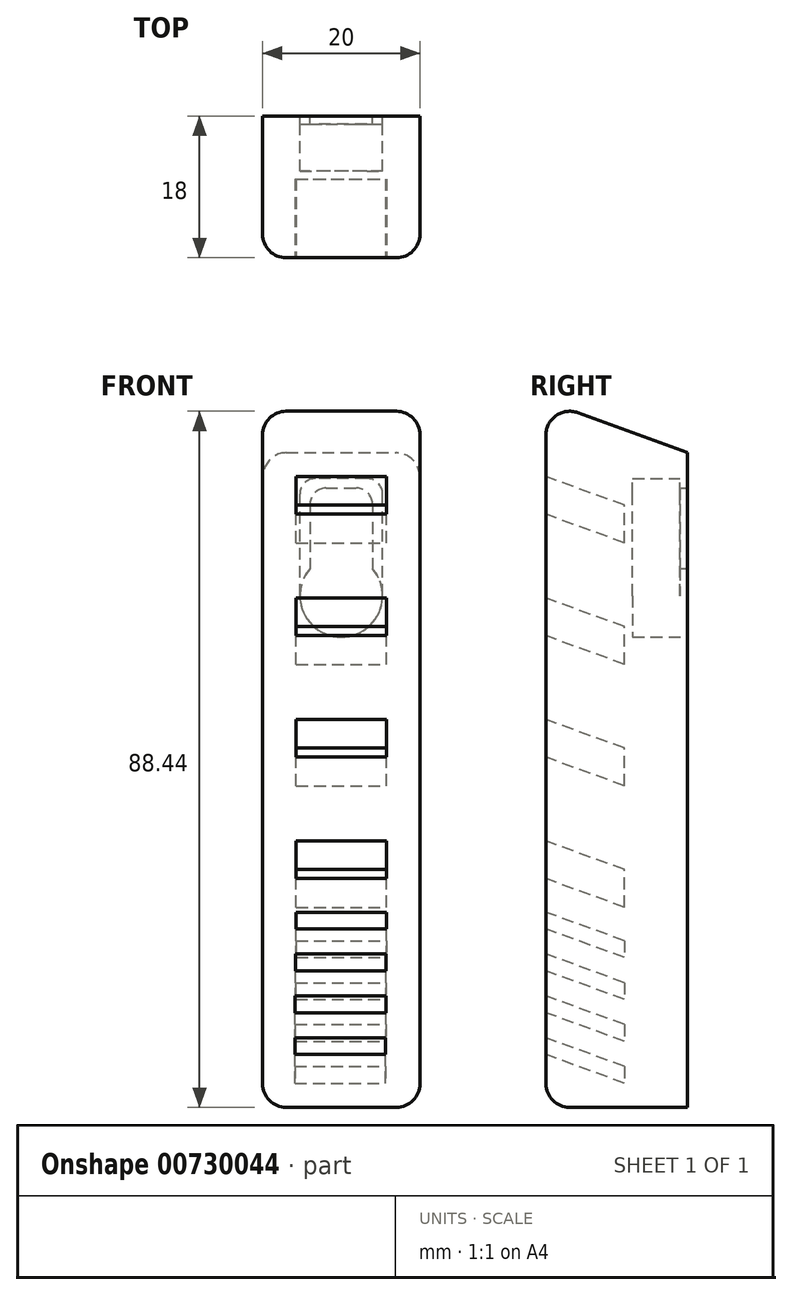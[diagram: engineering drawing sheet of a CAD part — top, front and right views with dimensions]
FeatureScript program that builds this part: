
annotation { "Feature Type Name" : "Feature", "Feature Type Description" : "" }
export const myFeature = defineFeature(function(context is Context, id is Id, definition is map)
    precondition{}
    {
        {
            var Q0;
            Q0=qCreatedBy(makeId("Front.planeOp"),FACE);
            var sketch = newSketch(context, id + "F0", { "sketchPlane" : qUnion([Q0])});
            skLineSegment(sketch, "E0.bottom", {"start": v(10, 45) * mm, "end": v(-10, 45) * mm});
            skLineSegment(sketch, "E0.top", {"start": v(10, -45) * mm, "end": v(-10, -45) * mm});
            skLineSegment(sketch, "E0.left", {"start": v(10, 45) * mm, "end": v(10, -45) * mm});
            skLineSegment(sketch, "E0.right", {"start": v(-10, 45) * mm, "end": v(-10, -45) * mm});
            skPoint(sketch, "E0.middle", {"position": v(0, 0) * mm});
            skSolve(sketch);
        }
        {
            var Q0;
            Q0 = qSketchRegion(id + "F0", true);
            extrude(context, id + "F1", {"entities" : qUnion([Q0]), "depth" : 18 * mm, "offsetDistance" : 25 * mm});
        }
        {
            var Q0;
            Q0=makeQuery(id+"F1.opExtrude","CAP_EDGE",EDGE,{"disambiguationData":[OSD([sQuery(id+"F0.wireOp",EDGE,"E0.bottom")])],"isStart":false});
            var Q1;
            Q1=makeQuery(id+"F1.opExtrude","CAP_FACE",FACE,{"disambiguationData":[OSD([sQuery(id+"F0.wireOp",EDGE,"E0.bottom"),sQuery(id+"F0.wireOp",EDGE,"E0.top"),sQuery(id+"F0.wireOp",EDGE,"E0.left"),sQuery(id+"F0.wireOp",EDGE,"E0.right")])],"isStart":false});
            cPlane(context, id + "F2", {"entities" : qUnion([Q0, Q1]), "cplaneType" : CPlaneType.LINE_ANGLE, "offset" : 25 * mm, "angle" : 20 * degree, "width" : 150 * mm, "height" : 150 * mm});
        }
        {
            var Q0;
            Q0=makeQuery(id+"F1.opExtrude","CAP_FACE",FACE,{"disambiguationData":[OSD([sQuery(id+"F0.wireOp",EDGE,"E0.bottom"),sQuery(id+"F0.wireOp",EDGE,"E0.top"),sQuery(id+"F0.wireOp",EDGE,"E0.left"),sQuery(id+"F0.wireOp",EDGE,"E0.right")])],"isStart":false});
            var sketch = newSketch(context, id + "F3", { "sketchPlane" : qUnion([Q0])});
            skLineSegment(sketch, "E1", {"start": v(0, 45) * mm, "end": v(0, 32.75) * mm, "construction": true});
            skLineSegment(sketch, "E2", {"start": v(0, -45) * mm, "end": v(0, -32.75) * mm, "construction": true});
            skSolve(sketch);
        }
        {
            var Q0;
            Q0=qCreatedBy(id+"F2.planeOp",FACE);
            var sketch = newSketch(context, id + "F4", { "sketchPlane" : qUnion([Q0])});
            skPoint(sketch, "E3", {"position": v(0, 24.62) * mm});
            skLineSegment(sketch, "E4.bottom", {"start": v(-5.75, 26.87) * mm, "end": v(5.75, 26.87) * mm});
            skLineSegment(sketch, "E4.top", {"start": v(-5.75, 22.37) * mm, "end": v(5.75, 22.37) * mm});
            skLineSegment(sketch, "E4.left", {"start": v(-5.75, 26.87) * mm, "end": v(-5.75, 22.37) * mm});
            skLineSegment(sketch, "E4.right", {"start": v(5.75, 26.87) * mm, "end": v(5.75, 22.37) * mm});
            skLineSegment(sketch, "E5.1.0.0", {"start": v(5.75, 12.37) * mm, "end": v(5.75, 7.87) * mm});
            skLineSegment(sketch, "E5.1.0.1", {"start": v(-5.75, 12.37) * mm, "end": v(5.75, 12.37) * mm});
            skLineSegment(sketch, "E5.1.0.2", {"start": v(-5.75, 12.37) * mm, "end": v(-5.75, 7.87) * mm});
            skLineSegment(sketch, "E5.1.0.3", {"start": v(-5.75, 7.87) * mm, "end": v(5.75, 7.87) * mm});
            skLineSegment(sketch, "E5.2.0.0", {"start": v(5.75, -2.13) * mm, "end": v(5.75, -6.63) * mm});
            skLineSegment(sketch, "E5.2.0.1", {"start": v(-5.75, -2.13) * mm, "end": v(5.75, -2.13) * mm});
            skLineSegment(sketch, "E5.2.0.2", {"start": v(-5.75, -2.13) * mm, "end": v(-5.75, -6.63) * mm});
            skLineSegment(sketch, "E5.2.0.3", {"start": v(-5.75, -6.63) * mm, "end": v(5.75, -6.63) * mm});
            skLineSegment(sketch, "E5.direction1", {"start": v(5.75, 22.37) * mm, "end": v(5.75, 7.87) * mm, "construction": true});
            skLineSegment(sketch, "E6.0.3.0", {"start": v(5.75, -16.63) * mm, "end": v(5.75, -21.13) * mm});
            skLineSegment(sketch, "E6.3.3.0", {"start": v(-5.75, -16.63) * mm, "end": v(5.75, -16.63) * mm});
            skLineSegment(sketch, "E6.6.3.0", {"start": v(-5.75, -16.63) * mm, "end": v(-5.75, -21.13) * mm});
            skLineSegment(sketch, "E6.9.3.0", {"start": v(-5.75, -21.13) * mm, "end": v(5.75, -21.13) * mm});
            skLineSegment(sketch, "E7", {"start": v(0, -21.13) * mm, "end": v(0, -26.13) * mm, "construction": true});
            skLineSegment(sketch, "E8.bottom", {"start": v(-5.75, -27.13) * mm, "end": v(5.75, -27.13) * mm});
            skLineSegment(sketch, "E8.top", {"start": v(-5.75, -25.13) * mm, "end": v(5.75, -25.13) * mm});
            skLineSegment(sketch, "E8.left", {"start": v(-5.75, -27.13) * mm, "end": v(-5.75, -25.13) * mm});
            skLineSegment(sketch, "E8.right", {"start": v(5.75, -27.13) * mm, "end": v(5.75, -25.13) * mm});
            skPoint(sketch, "E8.middle", {"position": v(0, -26.13) * mm});
            skLineSegment(sketch, "E9.1.0.0", {"start": v(5.8, -32.13) * mm, "end": v(5.8, -30.13) * mm});
            skLineSegment(sketch, "E9.1.0.1", {"start": v(-5.7, -30.13) * mm, "end": v(5.8, -30.13) * mm});
            skLineSegment(sketch, "E9.1.0.2", {"start": v(-5.7, -32.13) * mm, "end": v(-5.7, -30.13) * mm});
            skLineSegment(sketch, "E9.1.0.3", {"start": v(-5.7, -32.13) * mm, "end": v(5.8, -32.13) * mm});
            skLineSegment(sketch, "E9.2.0.0", {"start": v(5.85, -37.13) * mm, "end": v(5.85, -35.13) * mm});
            skLineSegment(sketch, "E9.2.0.1", {"start": v(-5.65, -35.13) * mm, "end": v(5.85, -35.13) * mm});
            skLineSegment(sketch, "E9.2.0.2", {"start": v(-5.65, -37.13) * mm, "end": v(-5.65, -35.13) * mm});
            skLineSegment(sketch, "E9.2.0.3", {"start": v(-5.65, -37.13) * mm, "end": v(5.85, -37.13) * mm});
            skLineSegment(sketch, "E9.3.0.0", {"start": v(5.9, -42.13) * mm, "end": v(5.9, -40.13) * mm});
            skLineSegment(sketch, "E9.3.0.1", {"start": v(-5.6, -40.13) * mm, "end": v(5.9, -40.13) * mm});
            skLineSegment(sketch, "E9.3.0.2", {"start": v(-5.6, -42.13) * mm, "end": v(-5.6, -40.13) * mm});
            skLineSegment(sketch, "E9.3.0.3", {"start": v(-5.6, -42.13) * mm, "end": v(5.9, -42.13) * mm});
            skLineSegment(sketch, "E9.direction1", {"start": v(5.75, -27.13) * mm, "end": v(5.8, -32.13) * mm, "construction": true});
            skSolve(sketch);
        }
        {
            var Q0;
            Q0=makeQuery(id+"F3.imprint","IMPRINT",FACE,{"disambiguationData":[TD([[makeQuery(id+"F3.imprint","IMPRINT",EDGE,{"derivedFrom":makeQuery(id+"F1.opExtrude","CAP_EDGE",EDGE,{"disambiguationData":[OSD([sQuery(id+"F0.wireOp",EDGE,"E0.bottom")])],"isStart":false})}),1.0]])]});
            cPlane(context, id + "F5", {"entities" : qUnion([Q0]), "cplaneType" : CPlaneType.OFFSET, "offset" : 10 * mm, "oppositeDirection" : true, "width" : 150 * mm, "height" : 150 * mm});
        }
        {
            var Q0;
            Q0=makeQuery(id+"F4.imprint","IMPRINT",FACE,{"disambiguationData":[TD([[makeQuery(id+"F4.imprint","IMPRINT",EDGE,{"derivedFrom":sQuery(id+"F4.wireOp",EDGE,"E4.bottom")}),-1.0]])]});
            var Q1;
            Q1=makeQuery(id+"F4.imprint","IMPRINT",FACE,{"disambiguationData":[TD([[makeQuery(id+"F4.imprint","IMPRINT",EDGE,{"derivedFrom":sQuery(id+"F4.wireOp",EDGE,"E5.1.0.0")}),-1.0]])]});
            var Q2;
            Q2=makeQuery(id+"F4.imprint","IMPRINT",FACE,{"disambiguationData":[TD([[makeQuery(id+"F4.imprint","IMPRINT",EDGE,{"derivedFrom":sQuery(id+"F4.wireOp",EDGE,"E5.2.0.0")}),-1.0]])]});
            var Q3;
            Q3=makeQuery(id+"F4.imprint","IMPRINT",FACE,{"disambiguationData":[TD([[makeQuery(id+"F4.imprint","IMPRINT",EDGE,{"derivedFrom":sQuery(id+"F4.wireOp",EDGE,"E6.0.3.0")}),-1.0]])]});
            var Q4;
            Q4=makeQuery(id+"F4.imprint","IMPRINT",FACE,{"disambiguationData":[TD([[makeQuery(id+"F4.imprint","IMPRINT",EDGE,{"derivedFrom":sQuery(id+"F4.wireOp",EDGE,"E8.bottom")}),1.0]])]});
            var Q5;
            Q5=makeQuery(id+"F4.imprint","IMPRINT",FACE,{"disambiguationData":[TD([[makeQuery(id+"F4.imprint","IMPRINT",EDGE,{"derivedFrom":sQuery(id+"F4.wireOp",EDGE,"E9.1.0.0")}),1.0]])]});
            var Q6;
            Q6=makeQuery(id+"F4.imprint","IMPRINT",FACE,{"disambiguationData":[TD([[makeQuery(id+"F4.imprint","IMPRINT",EDGE,{"derivedFrom":sQuery(id+"F4.wireOp",EDGE,"E9.2.0.0")}),1.0]])]});
            var Q7;
            Q7=makeQuery(id+"F4.imprint","IMPRINT",FACE,{"disambiguationData":[TD([[makeQuery(id+"F4.imprint","IMPRINT",EDGE,{"derivedFrom":sQuery(id+"F4.wireOp",EDGE,"E9.3.0.0")}),1.0]])]});
            var Q8;
            Q8=qCreatedBy(id+"F5.planeOp",FACE);
            extrude(context, id + "F6", {"entities" : qUnion([Q0, Q1, Q2, Q3, Q4, Q5, Q6, Q7]), "operationType" : NewBodyOperationType.REMOVE, "endBound" : BoundingType.UP_TO_SURFACE, "depth" : 25 * mm, "endBoundEntityFace" : qUnion([Q8]), "offsetDistance" : 25 * mm});
        }
        {
            var Q0;
            Q0=makeQuery(id+"F6.boolean.opBoolean","COPY",FACE,{"derivedFrom":makeQuery(id+"F6.opExtrude","SWEPT_FACE",FACE,{"disambiguationData":[OSD([sQuery(id+"F4.wireOp",EDGE,"E4.bottom")])]})});
            cPlane(context, id + "F7", {"entities" : qUnion([Q0]), "cplaneType" : CPlaneType.OFFSET, "offset" : 9 * mm, "oppositeDirection" : true, "width" : 150 * mm, "height" : 150 * mm});
        }
        {
            var Q0;
            Q0=qCreatedBy(id+"F7.planeOp",FACE);
            var sketch = newSketch(context, id + "F8", { "sketchPlane" : qUnion([Q0])});
            skLineSegment(sketch, "E10.bottom", {"start": v(-21.78, 0) * mm, "end": v(21.78, 0) * mm});
            skLineSegment(sketch, "E10.top", {"start": v(-21.78, 43.13) * mm, "end": v(21.78, 43.13) * mm});
            skLineSegment(sketch, "E10.left", {"start": v(-21.78, 0) * mm, "end": v(-21.78, 43.13) * mm});
            skLineSegment(sketch, "E10.right", {"start": v(21.78, 0) * mm, "end": v(21.78, 43.13) * mm});
            skPoint(sketch, "E10.middle", {"position": v(0, 21.57) * mm});
            skSolve(sketch);
        }
        {
            var Q0;
            Q0=makeQuery(id+"F8.imprint","IMPRINT",FACE,{"disambiguationData":[TD([[makeQuery(id+"F8.imprint","IMPRINT",EDGE,{"derivedFrom":sQuery(id+"F8.wireOp",EDGE,"E10.bottom")}),1.0]])]});
            extrude(context, id + "F9", {"entities" : qUnion([Q0]), "operationType" : NewBodyOperationType.REMOVE, "oppositeDirection" : true, "depth" : 16.4 * mm, "offsetDistance" : 25 * mm});
        }
        {
            var Q0;
            Q0=makeQuery(id+"F1.opExtrude","CAP_EDGE",EDGE,{"disambiguationData":[OSD([sQuery(id+"F0.wireOp",EDGE,"E0.right")])],"isStart":false});
            var Q1;
            Q1=makeQuery(id+"F9.boolean.opBoolean","INTERSECT",EDGE,{"derivedFrom":[makeQuery(id+"F1.opExtrude","CAP_FACE",FACE,{"disambiguationData":[OSD([sQuery(id+"F0.wireOp",EDGE,"E0.bottom"),sQuery(id+"F0.wireOp",EDGE,"E0.top"),sQuery(id+"F0.wireOp",EDGE,"E0.left"),sQuery(id+"F0.wireOp",EDGE,"E0.right")])],"isStart":false}),makeQuery(id+"F9.opExtrude","CAP_FACE",FACE,{"disambiguationData":[OSD([sQuery(id+"F8.wireOp",EDGE,"E10.bottom"),sQuery(id+"F8.wireOp",EDGE,"E10.top"),sQuery(id+"F8.wireOp",EDGE,"E10.left"),sQuery(id+"F8.wireOp",EDGE,"E10.right")])],"isStart":true})]});
            var Q2;
            Q2=makeQuery(id+"F1.opExtrude","CAP_EDGE",EDGE,{"disambiguationData":[OSD([sQuery(id+"F0.wireOp",EDGE,"E0.left")])],"isStart":false});
            var Q3;
            Q3=makeQuery(id+"F1.opExtrude","CAP_EDGE",EDGE,{"disambiguationData":[OSD([sQuery(id+"F0.wireOp",EDGE,"E0.top")])],"isStart":false});
            var Q4;
            Q4=makeQuery(id+"F9.boolean.opBoolean","INTERSECT",EDGE,{"derivedFrom":[makeQuery(id+"F1.opExtrude","SWEPT_FACE",FACE,{"disambiguationData":[OSD([sQuery(id+"F0.wireOp",EDGE,"E0.right")])]}),makeQuery(id+"F9.opExtrude","CAP_FACE",FACE,{"disambiguationData":[OSD([sQuery(id+"F8.wireOp",EDGE,"E10.bottom"),sQuery(id+"F8.wireOp",EDGE,"E10.top"),sQuery(id+"F8.wireOp",EDGE,"E10.left"),sQuery(id+"F8.wireOp",EDGE,"E10.right")])],"isStart":true})]});
            var Q5;
            Q5=makeQuery(id+"F9.boolean.opBoolean","INTERSECT",EDGE,{"derivedFrom":[makeQuery(id+"F1.opExtrude","SWEPT_FACE",FACE,{"disambiguationData":[OSD([sQuery(id+"F0.wireOp",EDGE,"E0.left")])]}),makeQuery(id+"F9.opExtrude","CAP_FACE",FACE,{"disambiguationData":[OSD([sQuery(id+"F8.wireOp",EDGE,"E10.bottom"),sQuery(id+"F8.wireOp",EDGE,"E10.top"),sQuery(id+"F8.wireOp",EDGE,"E10.left"),sQuery(id+"F8.wireOp",EDGE,"E10.right")])],"isStart":true})]});
            var Q6;
            Q6=makeQuery(id+"F1.opExtrude","SWEPT_EDGE",EDGE,{"disambiguationData":[OSD([sQuery(id+"F0.wireOp",EDGE,"E0.top"),sQuery(id+"F0.wireOp",EDGE,"E0.right")])]});
            var Q7;
            Q7=makeQuery(id+"F1.opExtrude","SWEPT_EDGE",EDGE,{"disambiguationData":[OSD([sQuery(id+"F0.wireOp",EDGE,"E0.top"),sQuery(id+"F0.wireOp",EDGE,"E0.left")])]});
            fillet(context, id + "F10", {"entities" : qUnion([Q0, Q1, Q2, Q3, Q4, Q5, Q6, Q7]), "radius" : 3 * mm, "tangentPropagation" : true, "allowEdgeOverflow" : false});
        }
        {
            var Q0;
            Q0=makeQuery(id+"F1.opExtrude","CAP_FACE",FACE,{"disambiguationData":[OSD([sQuery(id+"F0.wireOp",EDGE,"E0.bottom"),sQuery(id+"F0.wireOp",EDGE,"E0.top"),sQuery(id+"F0.wireOp",EDGE,"E0.left"),sQuery(id+"F0.wireOp",EDGE,"E0.right")])],"isStart":true});
            var sketch = newSketch(context, id + "F11", { "sketchPlane" : qUnion([Q0])});
            skCircle(sketch, "E11", {"center": v(0, 20) * mm, "radius": 5.25 * mm});
            skLineSegment(sketch, "E12.bottom", {"start": v(1.96, 33.68) * mm, "end": v(-1.96, 33.68) * mm});
            skLineSegment(sketch, "E12.left", {"start": v(3.96, 31.68) * mm, "end": v(3.96, 23.45) * mm});
            skLineSegment(sketch, "E12.right", {"start": v(-3.96, 31.68) * mm, "end": v(-3.96, 23.45) * mm});
            skPoint(sketch, "E13.visualSharp", {"position": v(-3.96, 33.68) * mm});
            skArc(sketch, "E13.filletArc", {"start": v(-1.96, 33.68) * mm, "mid": v(-3.37, 33.09) * mm, "end": v(-3.96, 31.68) * mm});
            skPoint(sketch, "E14.visualSharp", {"position": v(3.96, 33.68) * mm});
            skArc(sketch, "E14.filletArc", {"start": v(3.96, 31.68) * mm, "mid": v(3.37, 33.09) * mm, "end": v(1.96, 33.68) * mm});
            skLineSegment(sketch, "E15", {"start": v(5.25, 20) * mm, "end": v(5.25, 32.9) * mm});
            skPoint(sketch, "E16", {"position": v(5.25, 20) * mm});
            skLineSegment(sketch, "E17", {"start": v(0, 33.68) * mm, "end": v(0, 28.15) * mm, "construction": true});
            skLineSegment(sketch, "E18.MirrorCS", {"start": v(-5.25, 20) * mm, "end": v(-5.25, 32.9) * mm});
            skLineSegment(sketch, "E19", {"start": v(-3.25, 34.9) * mm, "end": v(3.25, 34.9) * mm});
            skPoint(sketch, "E20.visualSharp", {"position": v(-5.25, 34.9) * mm});
            skArc(sketch, "E20.filletArc", {"start": v(-3.25, 34.9) * mm, "mid": v(-4.66, 34.31) * mm, "end": v(-5.25, 32.9) * mm});
            skPoint(sketch, "E21.visualSharp", {"position": v(5.25, 34.9) * mm});
            skArc(sketch, "E21.filletArc", {"start": v(5.25, 32.9) * mm, "mid": v(4.66, 34.31) * mm, "end": v(3.25, 34.9) * mm});
            skSolve(sketch);
        }
        {
            var Q0;
            Q0 = qSketchRegion(id + "F11", true);
            var Q1;
            Q1=makeQuery(id+"F11.imprint","IMPRINT",FACE,{"disambiguationData":[TD([[makeQuery(id+"F11.imprint","IMPRINT",EDGE,{"derivedFrom":sQuery(id+"F11.wireOp",EDGE,"E12.bottom")}),1.0]])]});
            extrude(context, id + "F12", {"entities" : qUnion([Q0, Q1]), "operationType" : NewBodyOperationType.REMOVE, "oppositeDirection" : true, "depth" : 7 * mm, "offsetDistance" : 25 * mm});
        }
        {
            var Q0;
            Q0=makeQuery(id+"F11.imprint","IMPRINT",FACE,{"disambiguationData":[TD([[makeQuery(id+"F11.imprint","IMPRINT",EDGE,{"derivedFrom":sQuery(id+"F11.wireOp",EDGE,"E12.bottom")}),-1.0]])]});
            extrude(context, id + "F13", {"entities" : qUnion([Q0]), "operationType" : NewBodyOperationType.ADD, "oppositeDirection" : true, "depth" : 1 * mm, "offsetDistance" : 25 * mm});
        }
    });
